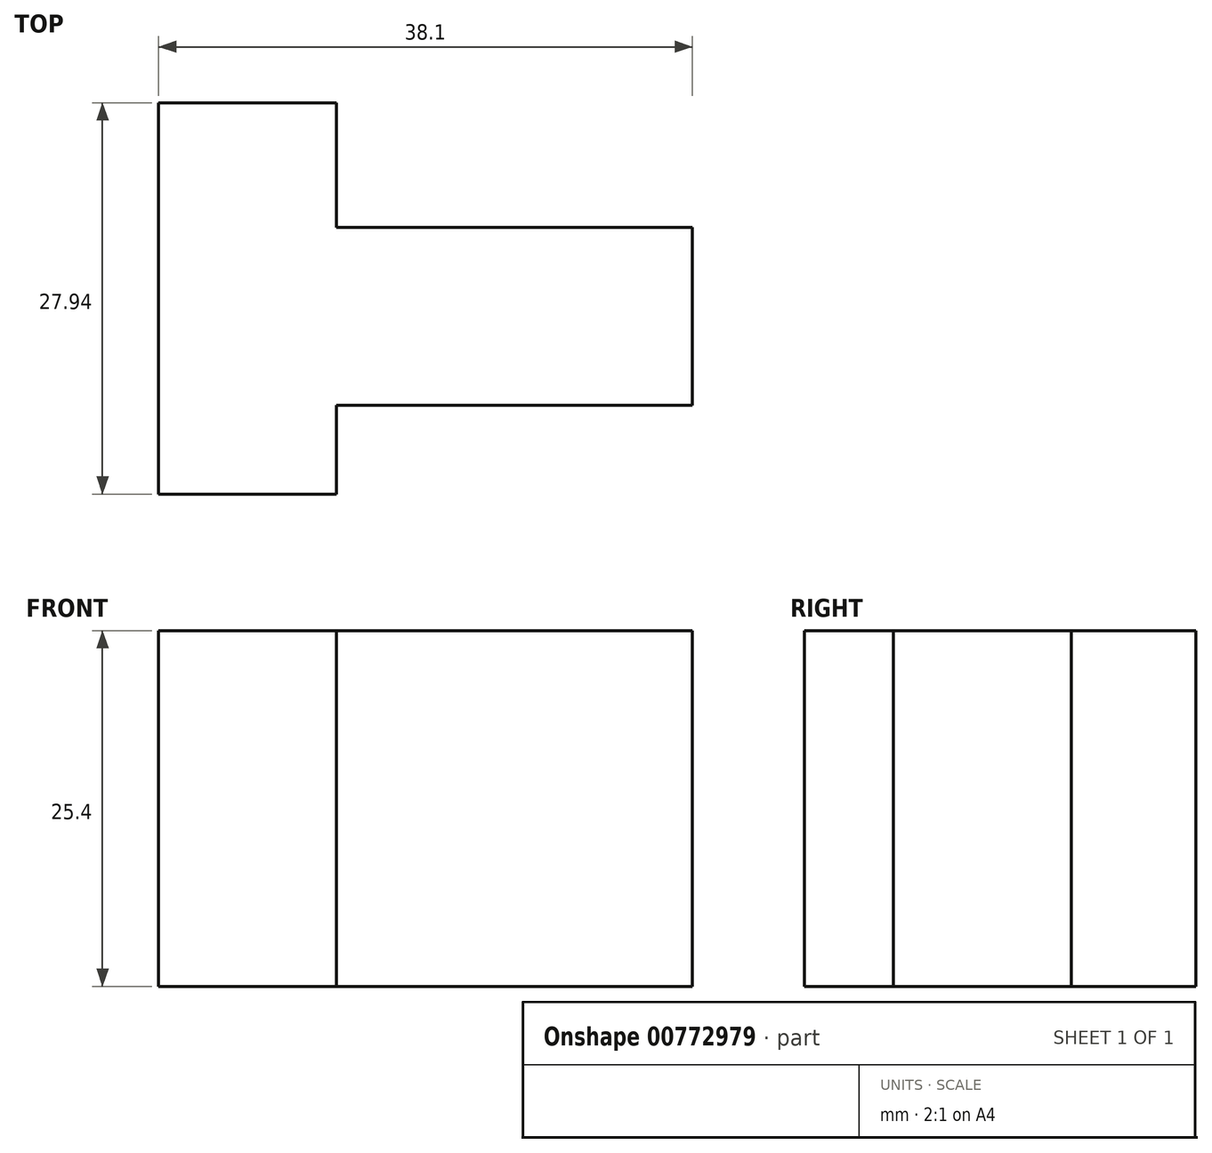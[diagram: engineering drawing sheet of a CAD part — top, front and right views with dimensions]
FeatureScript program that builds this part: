
annotation { "Feature Type Name" : "Feature", "Feature Type Description" : "" }
export const myFeature = defineFeature(function(context is Context, id is Id, definition is map)
    precondition{}
    {
        {
            var Q0;
            Q0=qCreatedBy(makeId("Top.planeOp"),FACE);
            var sketch = newSketch(context, id + "F0", { "sketchPlane" : qUnion([Q0])});
            skLineSegment(sketch, "E0", {"start": v(0, 0) * mm, "end": v(12.7, 0) * mm});
            skLineSegment(sketch, "E1", {"start": v(12.7, 0) * mm, "end": v(12.7, 6.35) * mm});
            skLineSegment(sketch, "E2", {"start": v(12.7, 6.35) * mm, "end": v(38.1, 6.35) * mm});
            skLineSegment(sketch, "E3", {"start": v(38.1, 6.35) * mm, "end": v(38.1, 19.05) * mm});
            skLineSegment(sketch, "E4", {"start": v(38.1, 19.05) * mm, "end": v(12.7, 19.05) * mm});
            skLineSegment(sketch, "E5", {"start": v(12.7, 19.05) * mm, "end": v(12.7, 27.94) * mm});
            skLineSegment(sketch, "E6", {"start": v(12.7, 27.94) * mm, "end": v(0, 27.94) * mm});
            skLineSegment(sketch, "E7", {"start": v(0, 27.94) * mm, "end": v(0, 0) * mm});
            skSolve(sketch);
        }
        {
            var Q0;
            Q0=makeQuery(id+"F0.imprint","IMPRINT",FACE,{"disambiguationData":[TD([[makeQuery(id+"F0.imprint","IMPRINT",EDGE,{"derivedFrom":sQuery(id+"F0.wireOp",EDGE,"E0")}),1.0]])]});
            extrude(context, id + "F1", {"entities" : qUnion([Q0]), "depth" : 25.4 * mm, "offsetDistance" : 25.4 * mm});
        }
    });
